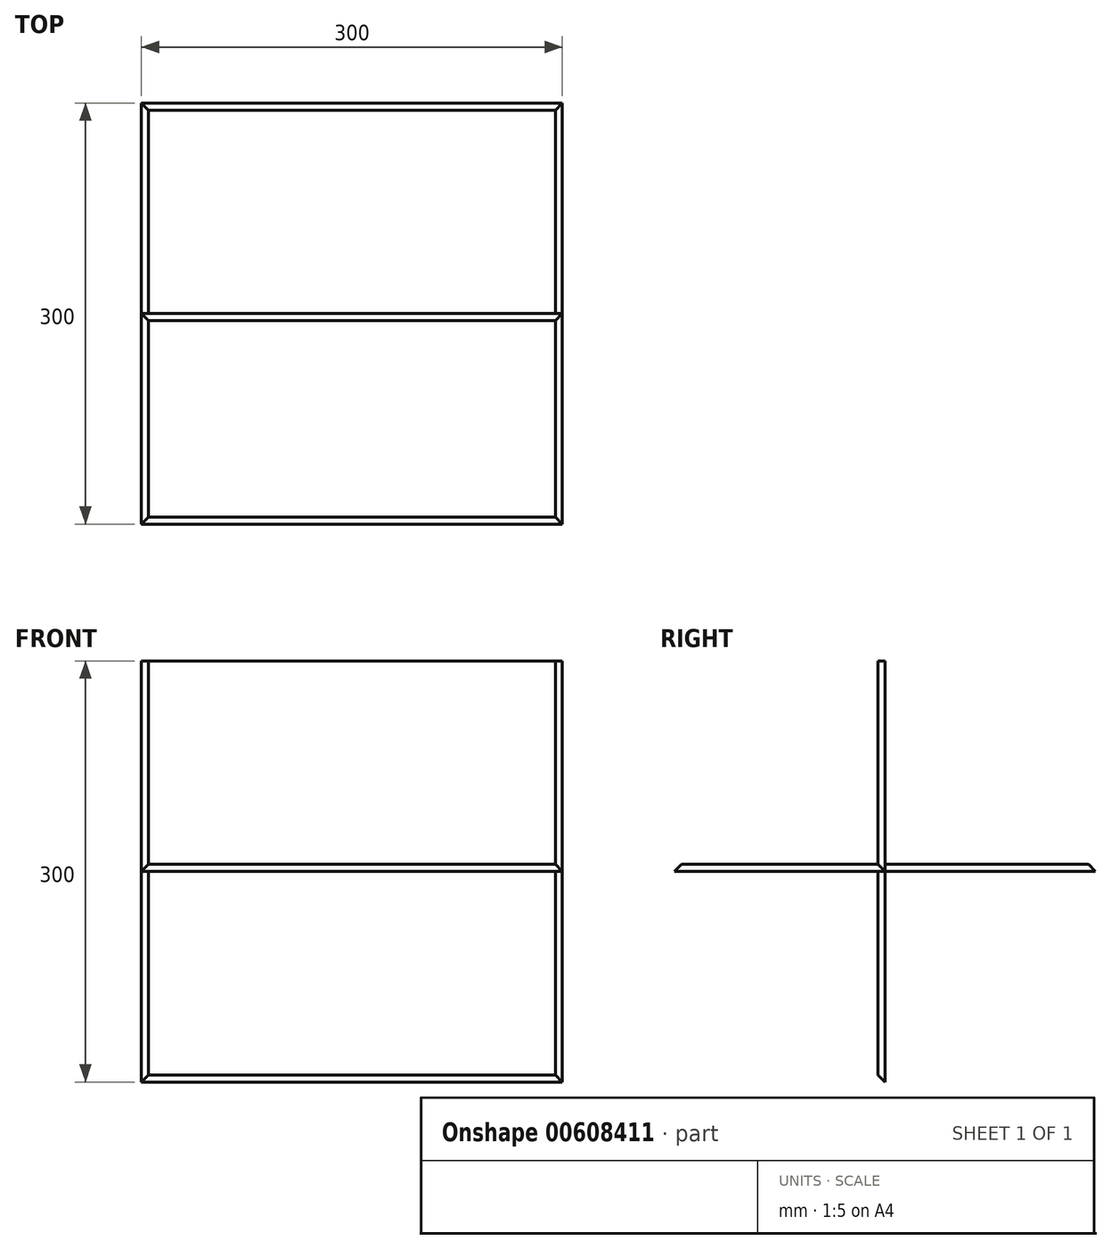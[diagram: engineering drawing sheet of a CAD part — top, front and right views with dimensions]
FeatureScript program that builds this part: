
annotation { "Feature Type Name" : "Feature", "Feature Type Description" : "" }
export const myFeature = defineFeature(function(context is Context, id is Id, definition is map)
    precondition{}
    {
        {
            var Q0;
            Q0=qCreatedBy(makeId("Top.planeOp"),FACE);
            var sketch = newSketch(context, id + "F0", { "sketchPlane" : qUnion([Q0])});
            skLineSegment(sketch, "E0.bottom", {"start": v(150, 150) * mm, "end": v(-150, 150) * mm});
            skLineSegment(sketch, "E0.top", {"start": v(150, -150) * mm, "end": v(-150, -150) * mm});
            skLineSegment(sketch, "E0.left", {"start": v(150, 150) * mm, "end": v(150, -150) * mm});
            skLineSegment(sketch, "E0.right", {"start": v(-150, 150) * mm, "end": v(-150, -150) * mm});
            skPoint(sketch, "E0.middle", {"position": v(0, 0) * mm});
            skSolve(sketch);
        }
        {
            var Q0;
            Q0 = qSketchRegion(id + "F0", true);
            extrude(context, id + "F1", {"entities" : qUnion([Q0]), "depth" : 5 * mm, "offsetDistance" : 25 * mm});
        }
        {
            var Q0;
            Q0=makeQuery(id+"F1.opExtrude","CAP_EDGE",EDGE,{"disambiguationData":[OSD([sQuery(id+"F0.wireOp",EDGE,"E0.right")])],"isStart":false});
            var Q1;
            Q1=makeQuery(id+"F1.opExtrude","CAP_EDGE",EDGE,{"disambiguationData":[OSD([sQuery(id+"F0.wireOp",EDGE,"E0.bottom")])],"isStart":false});
            var Q2;
            Q2=makeQuery(id+"F1.opExtrude","CAP_EDGE",EDGE,{"disambiguationData":[OSD([sQuery(id+"F0.wireOp",EDGE,"E0.left")])],"isStart":false});
            var Q3;
            Q3=makeQuery(id+"F1.opExtrude","CAP_EDGE",EDGE,{"disambiguationData":[OSD([sQuery(id+"F0.wireOp",EDGE,"E0.top")])],"isStart":false});
            chamfer(context, id + "F2", {"entities" : qUnion([Q0, Q1, Q2, Q3]), "width" : 5 * mm, "tangentPropagation" : true});
        }
        {
            var Q0;
            Q0=qCreatedBy(makeId("Front.planeOp"),FACE);
            var sketch = newSketch(context, id + "F3", { "sketchPlane" : qUnion([Q0])});
            skLineSegment(sketch, "E1.bottom", {"start": v(150, 150) * mm, "end": v(-150, 150) * mm});
            skLineSegment(sketch, "E1.top", {"start": v(150, -150) * mm, "end": v(-150, -150) * mm});
            skLineSegment(sketch, "E1.left", {"start": v(150, 150) * mm, "end": v(150, -150) * mm});
            skLineSegment(sketch, "E1.right", {"start": v(-150, 150) * mm, "end": v(-150, -150) * mm});
            skPoint(sketch, "E1.middle", {"position": v(0, 0) * mm});
            skSolve(sketch);
        }
        {
            var Q0;
            Q0 = qSketchRegion(id + "F3", true);
            extrude(context, id + "F4", {"entities" : qUnion([Q0]), "operationType" : NewBodyOperationType.ADD, "depth" : 5 * mm, "offsetDistance" : 25 * mm});
        }
        {
            var Q0;
            {var subQ0=sQuery(id+"F3.wireOp",EDGE,"E1.top");var subQ2=sQuery(id+"F3.wireOp",EDGE,"E1.right");Q0=makeQuery(id+"F4.boolean.opBoolean","SPLIT",EDGE,{"disambiguationData":[TD([makeQuery(id+"F4.opExtrude","SWEPT_FACE",FACE,{"disambiguationData":[OSD([subQ0])]})])],"derivedFrom":makeQuery(id+"F4.opExtrude","CAP_EDGE",EDGE,{"disambiguationData":[OSD([subQ2])],"isStart":false})});}
            var Q1;
            Q1=makeQuery(id+"F4.opExtrude","CAP_EDGE",EDGE,{"disambiguationData":[OSD([sQuery(id+"F3.wireOp",EDGE,"E1.top")])],"isStart":false});
            var Q2;
            {var subQ0=sQuery(id+"F3.wireOp",EDGE,"E1.top");var subQ2=sQuery(id+"F3.wireOp",EDGE,"E1.left");Q2=makeQuery(id+"F4.boolean.opBoolean","SPLIT",EDGE,{"disambiguationData":[TD([makeQuery(id+"F4.opExtrude","SWEPT_FACE",FACE,{"disambiguationData":[OSD([subQ0])]})])],"derivedFrom":makeQuery(id+"F4.opExtrude","CAP_EDGE",EDGE,{"disambiguationData":[OSD([subQ2])],"isStart":false})});}
            var Q3;
            {var subQ0=sQuery(id+"F3.wireOp",EDGE,"E1.bottom");var subQ2=sQuery(id+"F3.wireOp",EDGE,"E1.left");Q3=makeQuery(id+"F4.boolean.opBoolean","SPLIT",EDGE,{"disambiguationData":[TD([makeQuery(id+"F4.opExtrude","SWEPT_FACE",FACE,{"disambiguationData":[OSD([subQ0])]})])],"derivedFrom":makeQuery(id+"F4.opExtrude","CAP_EDGE",EDGE,{"disambiguationData":[OSD([subQ2])],"isStart":false})});}
            var Q4;
            {var subQ0=sQuery(id+"F3.wireOp",EDGE,"E1.bottom");var subQ2=sQuery(id+"F3.wireOp",EDGE,"E1.right");Q4=makeQuery(id+"F4.boolean.opBoolean","SPLIT",EDGE,{"disambiguationData":[TD([makeQuery(id+"F4.opExtrude","SWEPT_FACE",FACE,{"disambiguationData":[OSD([subQ0])]})])],"derivedFrom":makeQuery(id+"F4.opExtrude","CAP_EDGE",EDGE,{"disambiguationData":[OSD([subQ2])],"isStart":false})});}
            chamfer(context, id + "F5", {"entities" : qUnion([Q0, Q1, Q2, Q3, Q4]), "width" : 5 * mm, "tangentPropagation" : true});
        }
    });
